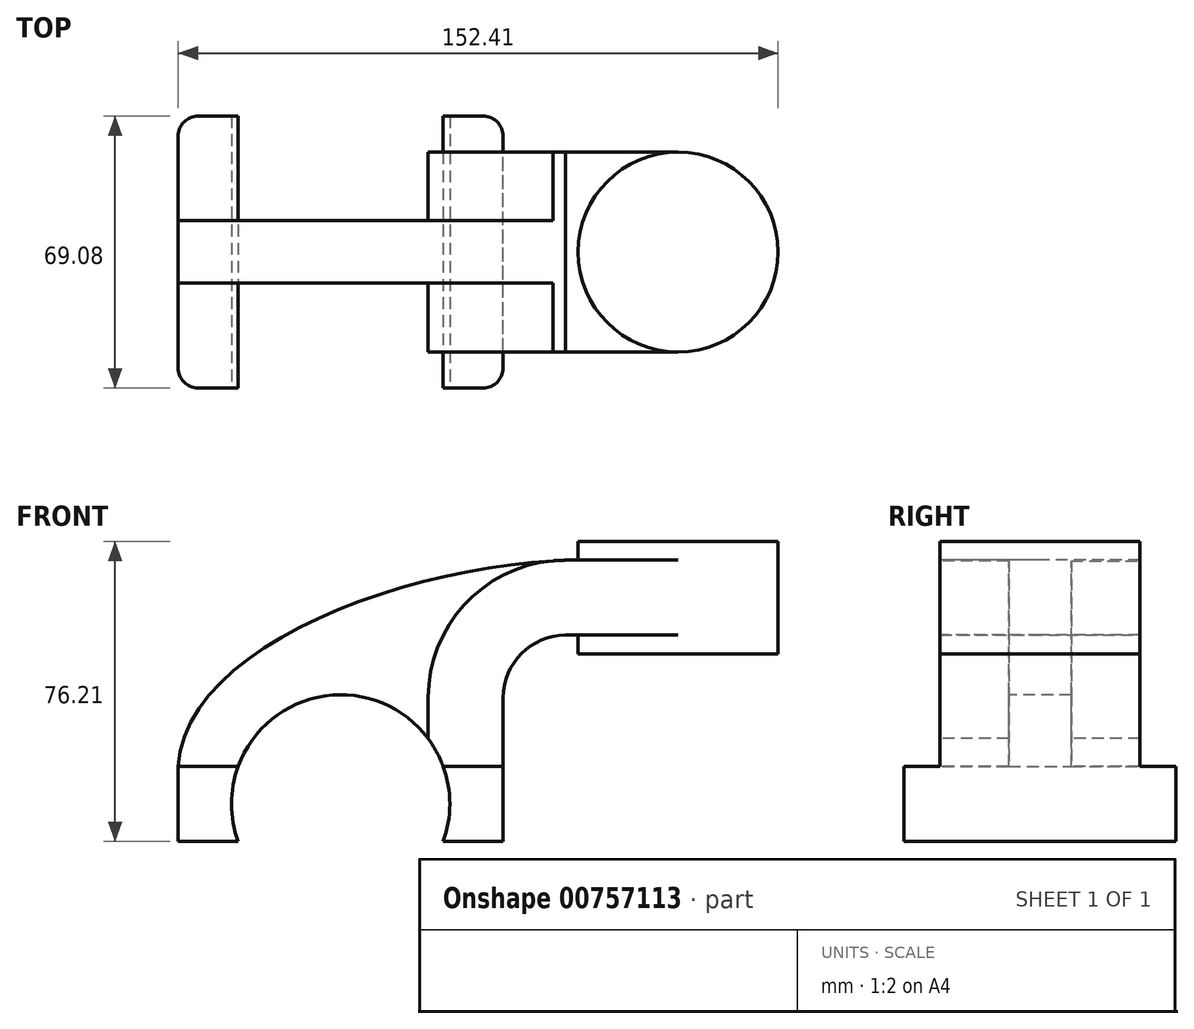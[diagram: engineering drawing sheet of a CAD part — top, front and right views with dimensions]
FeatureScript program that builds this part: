
annotation { "Feature Type Name" : "Feature", "Feature Type Description" : "" }
export const myFeature = defineFeature(function(context is Context, id is Id, definition is map)
    precondition{}
    {
        {
            var Q0;
            Q0=qCreatedBy(makeId("Front.planeOp"),FACE);
            var sketch = newSketch(context, id + "F0", { "sketchPlane" : qUnion([Q0])});
            skLineSegment(sketch, "E0.rect.bottom", {"start": v(-41.28, 9.52) * mm, "end": v(41.28, 9.52) * mm});
            skLineSegment(sketch, "E0.rect.top", {"start": v(-41.28, -9.52) * mm, "end": v(41.28, -9.52) * mm});
            skLineSegment(sketch, "E0.rect.left", {"start": v(-41.28, 9.52) * mm, "end": v(-41.28, -9.52) * mm});
            skLineSegment(sketch, "E0.rect.right", {"start": v(41.28, 9.52) * mm, "end": v(41.28, -9.52) * mm});
            skPoint(sketch, "E0.rect.middle", {"position": v(0, 0) * mm});
            skLineSegment(sketch, "E1", {"start": v(41.28, 9.52) * mm, "end": v(41.28, 27) * mm});
            skArc(sketch, "E2", {"start": v(41.28, 27) * mm, "mid": v(45.92, 38.23) * mm, "end": v(57.15, 42.88) * mm});
            skLineSegment(sketch, "E3", {"start": v(57.15, 42.88) * mm, "end": v(85.72, 42.88) * mm});
            skLineSegment(sketch, "E4.rect.bottom", {"start": v(60.32, 38.1) * mm, "end": v(111.12, 38.1) * mm});
            skLineSegment(sketch, "E4.rect.top", {"start": v(60.32, 66.68) * mm, "end": v(111.12, 66.68) * mm});
            skLineSegment(sketch, "E4.rect.left", {"start": v(60.32, 38.1) * mm, "end": v(60.32, 66.68) * mm});
            skLineSegment(sketch, "E4.rect.right", {"start": v(111.13, 38.1) * mm, "end": v(111.12, 66.68) * mm});
            skPoint(sketch, "E4.rect.middle", {"position": v(85.72, 52.39) * mm});
            skLineSegment(sketch, "E5.0", {"start": v(57.15, 61.93) * mm, "end": v(85.72, 61.93) * mm});
            skArc(sketch, "E5.1", {"start": v(22.23, 27) * mm, "mid": v(32.45, 51.7) * mm, "end": v(57.15, 61.93) * mm});
            skLineSegment(sketch, "E5.2", {"start": v(22.23, 9.52) * mm, "end": v(22.23, 27) * mm});
            skLineSegment(sketch, "E6", {"start": v(85.72, 38.1) * mm, "end": v(85.72, 66.68) * mm});
            skFitSpline(sketch, "E7", {"points": [v(-41.28, 9.53) * mm, v(57.15, 61.93) * mm], "startDerivative": vector(5.2, 92.34) * mm, "endDerivative": vector(120.92, 4.22) * mm});
            skSolve(sketch);
        }
        {
            var Q0;
            Q0=makeQuery(id+"F0.imprint","IMPRINT",FACE,{"disambiguationData":[TD([[makeQuery(id+"F0.imprint","IMPRINT",EDGE,{"derivedFrom":sQuery(id+"F0.wireOp",EDGE,"E0.rect.top")}),1.0]])]});
            extrude(context, id + "F1", {"entities" : qUnion([Q0]), "depth" : 69.1 * mm, "flatOperationType" : FlatOperationType.REMOVE, "offsetDistance" : 25.4 * mm, "domain" : OperationDomain.MODEL, "symmetric" : true});
        }
        {
            var Q0;
            {var subQ9=sQuery(id+"F0.wireOp",EDGE,"E1");Q0=makeQuery(id+"F0.imprint","IMPRINT",FACE,{"disambiguationData":[TD([[makeQuery(id+"F0.imprint","IMPRINT",EDGE,{"derivedFrom":subQ9}),1.0]])]});}
            var Q1;
            {var subQ0=sQuery(id+"F0.wireOp",EDGE,"E6");var subQ1=sQuery(id+"F0.wireOp",EDGE,"E3");var subQ2=makeQuery(id+"F0.imprint","INTERSECT",VERTEX,{"derivedFrom":[subQ1,subQ0]});Q1=makeQuery(id+"F0.imprint","IMPRINT",FACE,{"disambiguationData":[TD([[makeQuery(id+"F0.imprint","IMPRINT",EDGE,{"disambiguationData":[TD([[subQ2,1.0]])],"derivedFrom":subQ1}),1.0]])]});}
            extrude(context, id + "F2", {"entities" : qUnion([Q0, Q1]), "operationType" : NewBodyOperationType.ADD, "depth" : 50.8 * mm, "symmetric" : true});
        }
        {
            var Q0;
            {var subQ3=sQuery(id+"F0.wireOp",EDGE,"E5.2");Q0=makeQuery(id+"F0.imprint","IMPRINT",FACE,{"disambiguationData":[TD([[makeQuery(id+"F0.imprint","IMPRINT",EDGE,{"derivedFrom":subQ3}),1.0]])]});}
            extrude(context, id + "F3", {"entities" : qUnion([Q0]), "operationType" : NewBodyOperationType.ADD, "depth" : 15.88 * mm, "symmetric" : true});
        }
        {
            var Q0;
            {var subQ5=sQuery(id+"F0.wireOp",EDGE,"E4.rect.right");Q0=makeQuery(id+"F0.imprint","IMPRINT",FACE,{"disambiguationData":[TD([[makeQuery(id+"F0.imprint","IMPRINT",EDGE,{"derivedFrom":subQ5}),1.0]])]});}
            var Q1;
            Q1=sQuery(id+"F0.wireOp",EDGE,"E6");
            revolve(context, id + "F4", {"operationType" : NewBodyOperationType.ADD, "entities" : qUnion([Q0]), "axis" : qUnion([Q1]), "revolveType" : RevolveType.FULL});
        }
        {
            var Q0;
            Q0=makeQuery(id+"F1.opExtrude","CAP_EDGE",EDGE,{"disambiguationData":[OSD([sQuery(id+"F0.wireOp",EDGE,"E0.rect.right")])],"isStart":false});
            var Q1;
            Q1=makeQuery(id+"F1.opExtrude","CAP_EDGE",EDGE,{"disambiguationData":[OSD([sQuery(id+"F0.wireOp",EDGE,"E0.rect.left")])],"isStart":false});
            var Q2;
            Q2=makeQuery(id+"F1.opExtrude","CAP_EDGE",EDGE,{"disambiguationData":[OSD([sQuery(id+"F0.wireOp",EDGE,"E0.rect.right")])],"isStart":true});
            var Q3;
            Q3=makeQuery(id+"F1.opExtrude","CAP_EDGE",EDGE,{"disambiguationData":[OSD([sQuery(id+"F0.wireOp",EDGE,"E0.rect.left")])],"isStart":true});
            fillet(context, id + "F5", {"entities" : qUnion([Q0, Q1, Q2, Q3]), "radius" : 5.08 * mm, "tangentPropagation" : true, "allowEdgeOverflow" : false});
        }
        {
            var Q0;
            Q0=makeQuery(id+"F3.opExtrude","CAP_FACE",FACE,{"disambiguationData":[OSD([sQuery(id+"F0.wireOp",EDGE,"E0.rect.bottom"),sQuery(id+"F0.wireOp",EDGE,"E5.1"),sQuery(id+"F0.wireOp",EDGE,"E5.2"),sQuery(id+"F0.wireOp",EDGE,"E7")])],"isStart":false});
            var sketch = newSketch(context, id + "F6", { "sketchPlane" : qUnion([Q0])});
            skCircle(sketch, "E8", {"center": v(0, 0) * mm, "radius": 27.73 * mm});
            skSolve(sketch);
        }
        {
            var Q0;
            Q0 = qSketchRegion(id + "F6", true);
            extrude(context, id + "F7", {"entities" : qUnion([Q0]), "operationType" : NewBodyOperationType.REMOVE, "oppositeDirection" : true, "depth" : 92.46 * mm, "offsetDistance" : 25.4 * mm, "symmetric" : true});
        }
    });
